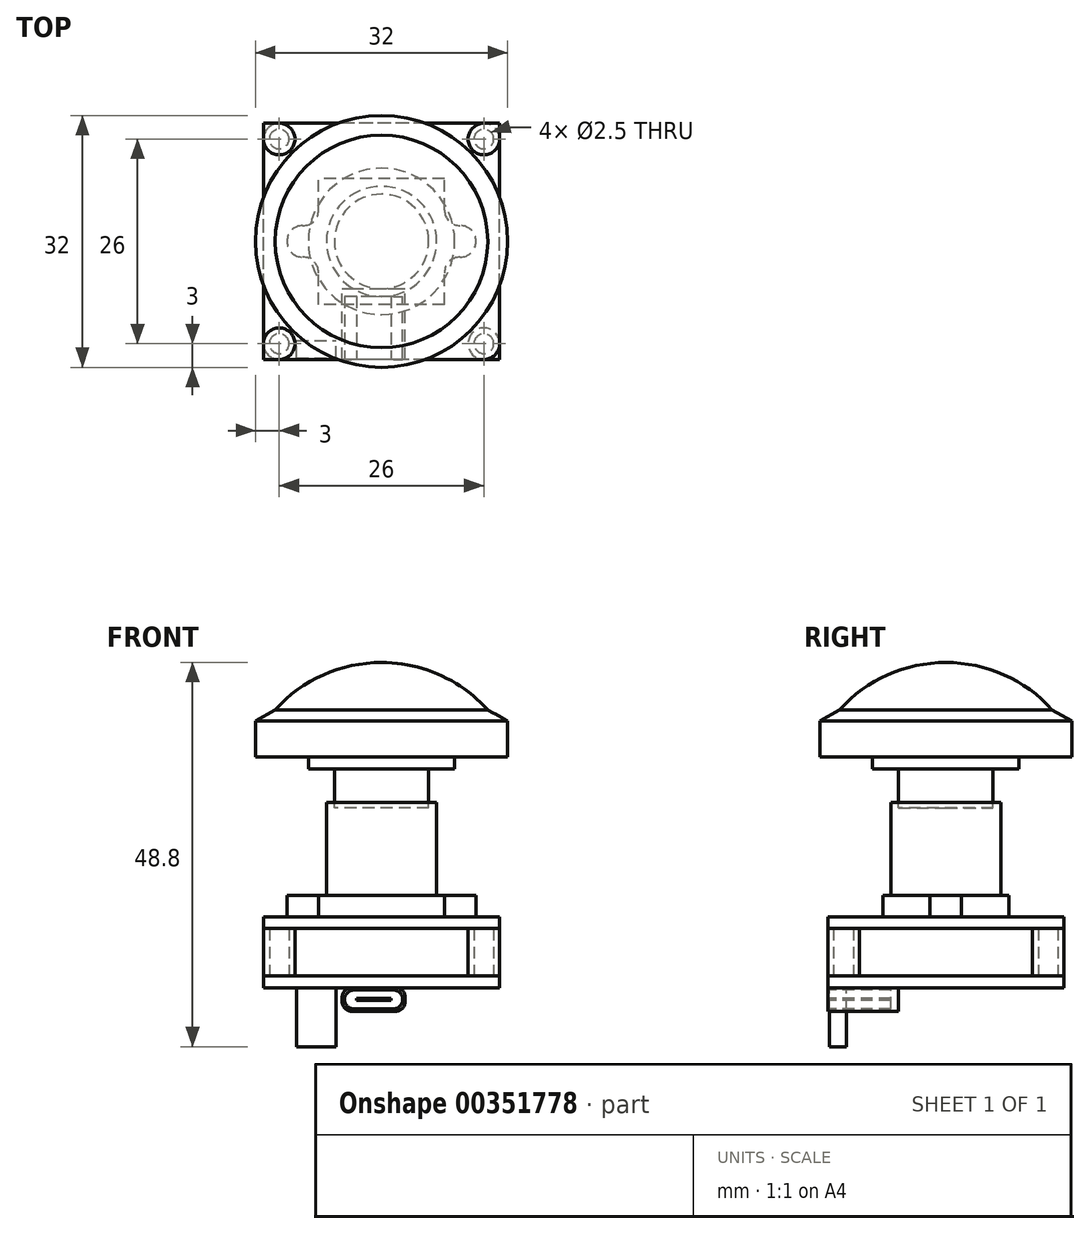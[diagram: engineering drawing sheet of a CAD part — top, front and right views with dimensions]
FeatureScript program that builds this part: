
annotation { "Feature Type Name" : "Feature", "Feature Type Description" : "" }
export const myFeature = defineFeature(function(context is Context, id is Id, definition is map)
    precondition{}
    {
        {
            var Q0;
            Q0=qCreatedBy(makeId("Top.planeOp"),FACE);
            var sketch = newSketch(context, id + "F0", { "sketchPlane" : qUnion([Q0])});
            skLineSegment(sketch, "E0.bottom", {"start": v(15, -15) * mm, "end": v(-15, -15) * mm});
            skLineSegment(sketch, "E0.top", {"start": v(15, 15) * mm, "end": v(-15, 15) * mm});
            skLineSegment(sketch, "E0.left", {"start": v(15, -15) * mm, "end": v(15, 15) * mm});
            skLineSegment(sketch, "E0.right", {"start": v(-15, -15) * mm, "end": v(-15, 15) * mm});
            skPoint(sketch, "E0.middle", {"position": v(0, 0) * mm});
            skSolve(sketch);
        }
        {
            var Q0;
            Q0=makeQuery(id+"F0.imprint","IMPRINT",FACE,{"disambiguationData":[TD([[makeQuery(id+"F0.imprint","IMPRINT",EDGE,{"derivedFrom":sQuery(id+"F0.wireOp",EDGE,"E0.bottom")}),-1.0]])]});
            extrude(context, id + "F1", {"entities" : qUnion([Q0]), "depth" : 1.5 * mm, "offsetDistance" : 25 * mm});
        }
        {
            var Q0;
            Q0=makeQuery(id+"F1.opExtrude","CAP_FACE",FACE,{"disambiguationData":[OSD([sQuery(id+"F0.wireOp",EDGE,"E0.bottom"),sQuery(id+"F0.wireOp",EDGE,"E0.top"),sQuery(id+"F0.wireOp",EDGE,"E0.left"),sQuery(id+"F0.wireOp",EDGE,"E0.right")])],"isStart":false});
            extrude(context, id + "F2", {"entities" : qUnion([Q0]), "operationType" : NewBodyOperationType.ADD, "depth" : 7.5 * mm, "offsetDistance" : 25 * mm, "hasSecondDirection" : true, "secondDirectionOppositeDirection" : false, "secondDirectionDepth" : 6 * mm});
        }
        {
            var Q0;
            Q0=makeQuery(id+"F1.opExtrude","CAP_FACE",FACE,{"disambiguationData":[OSD([sQuery(id+"F0.wireOp",EDGE,"E0.bottom"),sQuery(id+"F0.wireOp",EDGE,"E0.top"),sQuery(id+"F0.wireOp",EDGE,"E0.left"),sQuery(id+"F0.wireOp",EDGE,"E0.right")])],"isStart":false});
            var sketch = newSketch(context, id + "F3", { "sketchPlane" : qUnion([Q0])});
            skCircle(sketch, "E1", {"center": v(-13, 13) * mm, "radius": 1.25 * mm});
            skCircle(sketch, "E2", {"center": v(13, 13) * mm, "radius": 1.25 * mm});
            skCircle(sketch, "E3", {"center": v(-13, -13) * mm, "radius": 1.25 * mm});
            skCircle(sketch, "E4", {"center": v(13, 13) * mm, "radius": 2 * mm});
            skCircle(sketch, "E5", {"center": v(13, -13) * mm, "radius": 2 * mm});
            skCircle(sketch, "E6", {"center": v(-13, -13) * mm, "radius": 2 * mm});
            skCircle(sketch, "E7", {"center": v(-13, 13) * mm, "radius": 2 * mm});
            skCircle(sketch, "E8", {"center": v(13, -13) * mm, "radius": 1.25 * mm});
            skSolve(sketch);
        }
        {
            var Q0;
            Q0=makeQuery(id+"F3.imprint","IMPRINT",FACE,{"disambiguationData":[TD([[makeQuery(id+"F3.imprint","IMPRINT",EDGE,{"derivedFrom":sQuery(id+"F3.wireOp",EDGE,"E1")}),-1.0]])]});
            var Q1;
            Q1=makeQuery(id+"F3.imprint","IMPRINT",FACE,{"disambiguationData":[TD([[makeQuery(id+"F3.imprint","IMPRINT",EDGE,{"derivedFrom":sQuery(id+"F3.wireOp",EDGE,"E3")}),-1.0]])]});
            var Q2;
            Q2=makeQuery(id+"F3.imprint","IMPRINT",FACE,{"disambiguationData":[TD([[makeQuery(id+"F3.imprint","IMPRINT",EDGE,{"derivedFrom":sQuery(id+"F3.wireOp",EDGE,"E8")}),-1.0]])]});
            var Q3;
            Q3=makeQuery(id+"F3.imprint","IMPRINT",FACE,{"disambiguationData":[TD([[makeQuery(id+"F3.imprint","IMPRINT",EDGE,{"derivedFrom":sQuery(id+"F3.wireOp",EDGE,"E2")}),-1.0]])]});
            extrude(context, id + "F4", {"entities" : qUnion([Q0, Q1, Q2, Q3]), "depth" : 6 * mm, "offsetDistance" : 25 * mm});
        }
        {
            var Q0;
            Q0=makeQuery(id+"F2.opExtrude","CAP_FACE",FACE,{"disambiguationData":[OSD([sQuery(id+"F0.wireOp",EDGE,"E0.bottom"),sQuery(id+"F0.wireOp",EDGE,"E0.top"),sQuery(id+"F0.wireOp",EDGE,"E0.left"),sQuery(id+"F0.wireOp",EDGE,"E0.right")])],"isStart":false});
            var sketch = newSketch(context, id + "F5", { "sketchPlane" : qUnion([Q0])});
            skLineSegment(sketch, "E9.bottom", {"start": v(8, -8) * mm, "end": v(-8, -8) * mm});
            skLineSegment(sketch, "E9.top", {"start": v(8, 8) * mm, "end": v(-8, 8) * mm});
            skLineSegment(sketch, "E9.left", {"start": v(8, -8) * mm, "end": v(8, 8) * mm});
            skLineSegment(sketch, "E9.right", {"start": v(-8, -8) * mm, "end": v(-8, 8) * mm});
            skPoint(sketch, "E9.middle", {"position": v(0, 0) * mm});
            skLineSegment(sketch, "E10.bottom", {"start": v(-8, -2) * mm, "end": v(-12, -2) * mm});
            skLineSegment(sketch, "E10.top", {"start": v(-8, 2) * mm, "end": v(-12, 2) * mm});
            skLineSegment(sketch, "E10.left", {"start": v(-8, -2) * mm, "end": v(-8, 2) * mm});
            skLineSegment(sketch, "E10.right", {"start": v(-12, -2) * mm, "end": v(-12, 2) * mm});
            skPoint(sketch, "E10.middle", {"position": v(-10, 0) * mm});
            skPoint(sketch, "E10.middle.positionSnap0", {"position": v(-8, 0) * mm});
            skPoint(sketch, "E10.centerSnap0", {"position": v(-8, 0) * mm});
            skLineSegment(sketch, "E11.bottom", {"start": v(8, -2) * mm, "end": v(12, -2) * mm});
            skLineSegment(sketch, "E11.top", {"start": v(8, 2) * mm, "end": v(12, 2) * mm});
            skLineSegment(sketch, "E11.left", {"start": v(8, -2) * mm, "end": v(8, 2) * mm});
            skLineSegment(sketch, "E11.right", {"start": v(12, -2) * mm, "end": v(12, 2) * mm});
            skPoint(sketch, "E11.middle", {"position": v(10, 0) * mm});
            skCircle(sketch, "E12", {"center": v(0, 0) * mm, "radius": 7 * mm});
            skSolve(sketch);
        }
        {
            var Q0;
            Q0=makeQuery(id+"F5.imprint","IMPRINT",FACE,{"disambiguationData":[TD([[makeQuery(id+"F5.imprint","IMPRINT",EDGE,{"derivedFrom":sQuery(id+"F5.wireOp",EDGE,"E10.bottom")}),-1.0]])]});
            var Q1;
            {var subQ3=sQuery(id+"F5.wireOp",EDGE,"E9.bottom");Q1=makeQuery(id+"F5.imprint","IMPRINT",FACE,{"disambiguationData":[TD([[makeQuery(id+"F5.imprint","IMPRINT",EDGE,{"derivedFrom":subQ3}),-1.0]])]});}
            var Q2;
            Q2=makeQuery(id+"F5.imprint","IMPRINT",FACE,{"disambiguationData":[TD([[makeQuery(id+"F5.imprint","IMPRINT",EDGE,{"derivedFrom":sQuery(id+"F5.wireOp",EDGE,"E11.bottom")}),1.0]])]});
            var Q3;
            Q3=makeQuery(id+"F5.imprint","IMPRINT",FACE,{"disambiguationData":[TD([[makeQuery(id+"F5.imprint","IMPRINT",EDGE,{"derivedFrom":sQuery(id+"F5.wireOp",EDGE,"E12")}),1.0]])]});
            extrude(context, id + "F6", {"entities" : qUnion([Q0, Q1, Q2, Q3]), "depth" : 2.7 * mm, "offsetDistance" : 25 * mm});
        }
        {
            var Q0;
            Q0=makeQuery(id+"F6.opExtrude","SWEPT_EDGE",EDGE,{"disambiguationData":[OSD([sQuery(id+"F5.wireOp",EDGE,"E10.top"),sQuery(id+"F5.wireOp",EDGE,"E10.right")])]});
            var Q1;
            Q1=makeQuery(id+"F6.opExtrude","SWEPT_EDGE",EDGE,{"disambiguationData":[OSD([sQuery(id+"F5.wireOp",EDGE,"E10.bottom"),sQuery(id+"F5.wireOp",EDGE,"E10.right")])]});
            var Q2;
            Q2=makeQuery(id+"F6.opExtrude","SWEPT_EDGE",EDGE,{"disambiguationData":[OSD([sQuery(id+"F5.wireOp",EDGE,"E9.right"),sQuery(id+"F5.wireOp",EDGE,"E10.top"),sQuery(id+"F5.wireOp",EDGE,"E10.left")])]});
            var Q3;
            Q3=makeQuery(id+"F6.opExtrude","SWEPT_EDGE",EDGE,{"disambiguationData":[OSD([sQuery(id+"F5.wireOp",EDGE,"E9.right"),sQuery(id+"F5.wireOp",EDGE,"E10.bottom"),sQuery(id+"F5.wireOp",EDGE,"E10.left")])]});
            var Q4;
            Q4=makeQuery(id+"F6.opExtrude","SWEPT_EDGE",EDGE,{"disambiguationData":[OSD([sQuery(id+"F5.wireOp",EDGE,"E11.bottom"),sQuery(id+"F5.wireOp",EDGE,"E11.right")])]});
            var Q5;
            Q5=makeQuery(id+"F6.opExtrude","SWEPT_EDGE",EDGE,{"disambiguationData":[OSD([sQuery(id+"F5.wireOp",EDGE,"E9.left"),sQuery(id+"F5.wireOp",EDGE,"E11.bottom"),sQuery(id+"F5.wireOp",EDGE,"E11.left")])]});
            var Q6;
            Q6=makeQuery(id+"F6.opExtrude","SWEPT_EDGE",EDGE,{"disambiguationData":[OSD([sQuery(id+"F5.wireOp",EDGE,"E9.left"),sQuery(id+"F5.wireOp",EDGE,"E11.top"),sQuery(id+"F5.wireOp",EDGE,"E11.left")])]});
            var Q7;
            Q7=makeQuery(id+"F6.opExtrude","SWEPT_EDGE",EDGE,{"disambiguationData":[OSD([sQuery(id+"F5.wireOp",EDGE,"E11.top"),sQuery(id+"F5.wireOp",EDGE,"E11.right")])]});
            fillet(context, id + "F7", {"entities" : qUnion([Q0, Q1, Q2, Q3, Q4, Q5, Q6, Q7]), "radius" : 2 * mm, "tangentPropagation" : true, "allowEdgeOverflow" : false});
        }
        {
            var Q0;
            Q0=makeQuery(id+"F5.imprint","IMPRINT",FACE,{"disambiguationData":[TD([[makeQuery(id+"F5.imprint","IMPRINT",EDGE,{"derivedFrom":sQuery(id+"F5.wireOp",EDGE,"E12")}),1.0]])]});
            extrude(context, id + "F8", {"entities" : qUnion([Q0]), "operationType" : NewBodyOperationType.ADD, "depth" : 14.5 * mm, "offsetDistance" : 25 * mm});
        }
        {
            var Q0;
            Q0=qCreatedBy(makeId("Front.planeOp"),FACE);
            var sketch = newSketch(context, id + "F9", { "sketchPlane" : qUnion([Q0])});
            skLineSegment(sketch, "E13.bottom", {"start": v(0, 27.8) * mm, "end": v(-6, 27.8) * mm});
            skLineSegment(sketch, "E13.top", {"start": v(0, 22.8) * mm, "end": v(-6, 22.8) * mm});
            skLineSegment(sketch, "E13.left", {"start": v(0, 27.8) * mm, "end": v(0, 22.8) * mm});
            skLineSegment(sketch, "E13.right", {"start": v(-6, 27.8) * mm, "end": v(-6, 22.8) * mm});
            skLineSegment(sketch, "E14.bottom", {"start": v(0, 27.8) * mm, "end": v(-9.3, 27.8) * mm});
            skLineSegment(sketch, "E14.top", {"start": v(0, 29.3) * mm, "end": v(-9.3, 29.3) * mm});
            skLineSegment(sketch, "E14.left", {"start": v(0, 27.8) * mm, "end": v(0, 29.3) * mm});
            skLineSegment(sketch, "E14.right", {"start": v(-9.3, 27.8) * mm, "end": v(-9.3, 29.3) * mm});
            skLineSegment(sketch, "E15.bottom", {"start": v(0, 29.3) * mm, "end": v(-16, 29.3) * mm});
            skLineSegment(sketch, "E15.top", {"start": v(0, 35.3) * mm, "end": v(-13.5, 35.3) * mm});
            skLineSegment(sketch, "E15.left", {"start": v(0, 29.3) * mm, "end": v(0, 35.3) * mm});
            skLineSegment(sketch, "E15.right", {"start": v(-16, 29.3) * mm, "end": v(-16, 33.86) * mm});
            skLineSegment(sketch, "E16", {"start": v(-16, 33.86) * mm, "end": v(-13.5, 35.3) * mm});
            skArc(sketch, "E17", {"start": v(-13.5, 35.3) * mm, "mid": v(-7.39, 39.73) * mm, "end": v(0, 41.3) * mm});
            skLineSegment(sketch, "E18", {"start": v(0, 41.3) * mm, "end": v(0, 35.3) * mm});
            skSolve(sketch);
        }
        {
            var Q0;
            Q0=makeQuery(id+"F9.imprint","IMPRINT",FACE,{"disambiguationData":[TD([[makeQuery(id+"F9.imprint","IMPRINT",EDGE,{"derivedFrom":sQuery(id+"F9.wireOp",EDGE,"E15.top")}),-1.0]])]});
            var Q1;
            Q1=sQuery(id+"F9.wireOp",EDGE,"E13.left");
            revolve(context, id + "F10", {"surfaceOperationType" : NewSurfaceOperationType.NEW, "entities" : qUnion([Q0]), "axis" : qUnion([Q1]), "revolveType" : RevolveType.FULL});
        }
        {
            var Q0;
            Q0=makeQuery(id+"F9.imprint","IMPRINT",FACE,{"disambiguationData":[TD([[makeQuery(id+"F9.imprint","IMPRINT",EDGE,{"derivedFrom":sQuery(id+"F9.wireOp",EDGE,"E15.top")}),1.0]])]});
            var Q1;
            {var subQ1=sQuery(id+"F9.wireOp",EDGE,"E14.left");Q1=makeQuery(id+"F9.imprint","IMPRINT",FACE,{"disambiguationData":[TD([[makeQuery(id+"F9.imprint","IMPRINT",EDGE,{"derivedFrom":subQ1}),1.0]])]});}
            var Q2;
            Q2=makeQuery(id+"F9.imprint","IMPRINT",FACE,{"disambiguationData":[TD([[makeQuery(id+"F9.imprint","IMPRINT",EDGE,{"derivedFrom":sQuery(id+"F9.wireOp",EDGE,"E13.top")}),-1.0]])]});
            var Q3;
            Q3=sQuery(id+"F9.wireOp",EDGE,"E13.left");
            revolve(context, id + "F11", {"surfaceOperationType" : NewSurfaceOperationType.NEW, "entities" : qUnion([Q0, Q1, Q2]), "axis" : qUnion([Q3]), "revolveType" : RevolveType.FULL});
        }
        {
            var Q0;
            Q0=makeQuery(id+"F1.opExtrude","CAP_FACE",FACE,{"disambiguationData":[OSD([sQuery(id+"F0.wireOp",EDGE,"E0.bottom"),sQuery(id+"F0.wireOp",EDGE,"E0.top"),sQuery(id+"F0.wireOp",EDGE,"E0.left"),sQuery(id+"F0.wireOp",EDGE,"E0.right")])],"isStart":true});
            var sketch = newSketch(context, id + "F12", { "sketchPlane" : qUnion([Q0])});
            skLineSegment(sketch, "E19.bottom", {"start": v(-5, 15) * mm, "end": v(3, 15) * mm});
            skLineSegment(sketch, "E19.top", {"start": v(-5, 6) * mm, "end": v(3, 6) * mm});
            skLineSegment(sketch, "E19.left", {"start": v(-5, 15) * mm, "end": v(-5, 6) * mm});
            skLineSegment(sketch, "E19.right", {"start": v(3, 15) * mm, "end": v(3, 6) * mm});
            skSolve(sketch);
        }
        {
            var Q0;
            Q0=makeQuery(id+"F12.imprint","IMPRINT",FACE,{"disambiguationData":[TD([[makeQuery(id+"F12.imprint","IMPRINT",EDGE,{"derivedFrom":sQuery(id+"F12.wireOp",EDGE,"E19.bottom")}),1.0]])]});
            extrude(context, id + "F13", {"entities" : qUnion([Q0]), "depth" : 3 * mm, "offsetDistance" : 25 * mm});
        }
        {
            var Q0;
            Q0=makeQuery(id+"F13.opExtrude","SWEPT_FACE",FACE,{"disambiguationData":[OSD([sQuery(id+"F12.wireOp",EDGE,"E19.bottom")])]});
            var sketch = newSketch(context, id + "F14", { "sketchPlane" : qUnion([Q0])});
            skLineSegment(sketch, "E20.0", {"start": v(2.7, -2.7) * mm, "end": v(2.7, -0.3) * mm});
            skLineSegment(sketch, "E20.1", {"start": v(2.7, -2.7) * mm, "end": v(-4.7, -2.7) * mm});
            skLineSegment(sketch, "E20.2", {"start": v(-4.7, -2.7) * mm, "end": v(-4.7, -0.3) * mm});
            skLineSegment(sketch, "E20.3", {"start": v(2.7, -0.3) * mm, "end": v(-4.7, -0.3) * mm});
            skPoint(sketch, "E21.top.end.orphan", {"position": v(1.8, -1.8) * mm});
            skLineSegment(sketch, "E22.bottom", {"start": v(1.18, -1.65) * mm, "end": v(-3.18, -1.65) * mm});
            skLineSegment(sketch, "E22.top", {"start": v(1.18, -1.35) * mm, "end": v(-3.18, -1.35) * mm});
            skLineSegment(sketch, "E22.left", {"start": v(1.18, -1.65) * mm, "end": v(1.18, -1.35) * mm});
            skLineSegment(sketch, "E22.right", {"start": v(-3.18, -1.65) * mm, "end": v(-3.18, -1.35) * mm});
            skPoint(sketch, "E22.middle", {"position": v(-1, -1.5) * mm});
            skPoint(sketch, "E22.middle.positionSnap0", {"position": v(3, -1.5) * mm});
            skPoint(sketch, "E22.middle.positionSnap1", {"position": v(-1, 0) * mm});
            skPoint(sketch, "E22.centerSnap0", {"position": v(3, -1.5) * mm});
            skPoint(sketch, "E22.centerSnap1", {"position": v(-1, 0) * mm});
            skSolve(sketch);
        }
        {
            var Q0;
            Q0=makeQuery(id+"F14.imprint","IMPRINT",FACE,{"disambiguationData":[TD([[makeQuery(id+"F14.imprint","IMPRINT",EDGE,{"derivedFrom":sQuery(id+"F14.wireOp",EDGE,"E20.0")}),1.0]])]});
            extrude(context, id + "F15", {"entities" : qUnion([Q0]), "operationType" : NewBodyOperationType.REMOVE, "oppositeDirection" : true, "depth" : 8 * mm, "offsetDistance" : 25 * mm});
        }
        {
            var Q0;
            Q0=makeQuery(id+"F13.opExtrude","CAP_EDGE",EDGE,{"disambiguationData":[OSD([sQuery(id+"F12.wireOp",EDGE,"E19.left")])],"isStart":false});
            var Q1;
            Q1=makeQuery(id+"F13.opExtrude","CAP_EDGE",EDGE,{"disambiguationData":[OSD([sQuery(id+"F12.wireOp",EDGE,"E19.left")])],"isStart":true});
            var Q2;
            Q2=makeQuery(id+"F13.opExtrude","CAP_EDGE",EDGE,{"disambiguationData":[OSD([sQuery(id+"F12.wireOp",EDGE,"E19.right")])],"isStart":true});
            var Q3;
            Q3=makeQuery(id+"F13.opExtrude","CAP_EDGE",EDGE,{"disambiguationData":[OSD([sQuery(id+"F12.wireOp",EDGE,"E19.right")])],"isStart":false});
            var Q4;
            Q4=makeQuery(id+"F15.boolean.opBoolean","COPY",EDGE,{"derivedFrom":makeQuery(id+"F15.opExtrude","SWEPT_EDGE",EDGE,{"disambiguationData":[OSD([sQuery(id+"F14.wireOp",EDGE,"E20.2"),sQuery(id+"F14.wireOp",EDGE,"E20.3")])]})});
            var Q5;
            Q5=makeQuery(id+"F15.boolean.opBoolean","COPY",EDGE,{"derivedFrom":makeQuery(id+"F15.opExtrude","SWEPT_EDGE",EDGE,{"disambiguationData":[OSD([sQuery(id+"F14.wireOp",EDGE,"E20.0"),sQuery(id+"F14.wireOp",EDGE,"E20.3")])]})});
            var Q6;
            Q6=makeQuery(id+"F15.boolean.opBoolean","COPY",EDGE,{"derivedFrom":makeQuery(id+"F15.opExtrude","SWEPT_EDGE",EDGE,{"disambiguationData":[OSD([sQuery(id+"F14.wireOp",EDGE,"E20.0"),sQuery(id+"F14.wireOp",EDGE,"E20.1")])]})});
            var Q7;
            Q7=makeQuery(id+"F15.boolean.opBoolean","COPY",EDGE,{"derivedFrom":makeQuery(id+"F15.opExtrude","SWEPT_EDGE",EDGE,{"disambiguationData":[OSD([sQuery(id+"F14.wireOp",EDGE,"E20.1"),sQuery(id+"F14.wireOp",EDGE,"E20.2")])]})});
            fillet(context, id + "F16", {"entities" : qUnion([Q0, Q1, Q2, Q3, Q4, Q5, Q6, Q7]), "radius" : 1.2 * mm, "tangentPropagation" : true, "allowEdgeOverflow" : false});
        }
        {
            var Q0;
            Q0=makeQuery(id+"F1.opExtrude","CAP_FACE",FACE,{"disambiguationData":[OSD([sQuery(id+"F0.wireOp",EDGE,"E0.bottom"),sQuery(id+"F0.wireOp",EDGE,"E0.top"),sQuery(id+"F0.wireOp",EDGE,"E0.left"),sQuery(id+"F0.wireOp",EDGE,"E0.right")])],"isStart":true});
            var sketch = newSketch(context, id + "F17", { "sketchPlane" : qUnion([Q0])});
            skLineSegment(sketch, "E23.bottom", {"start": v(-10.8, 14.8) * mm, "end": v(-5.8, 14.8) * mm});
            skLineSegment(sketch, "E23.top", {"start": v(-10.8, 12.6) * mm, "end": v(-5.8, 12.6) * mm});
            skLineSegment(sketch, "E23.left", {"start": v(-10.8, 14.8) * mm, "end": v(-10.8, 12.6) * mm});
            skLineSegment(sketch, "E23.right", {"start": v(-5.8, 14.8) * mm, "end": v(-5.8, 12.6) * mm});
            skSolve(sketch);
        }
        {
            var Q0;
            Q0=makeQuery(id+"F17.imprint","IMPRINT",FACE,{"disambiguationData":[TD([[makeQuery(id+"F17.imprint","IMPRINT",EDGE,{"derivedFrom":sQuery(id+"F17.wireOp",EDGE,"E23.bottom")}),-1.0]])]});
            extrude(context, id + "F18", {"entities" : qUnion([Q0]), "depth" : 7.5 * mm, "offsetDistance" : 25 * mm});
        }
    });
